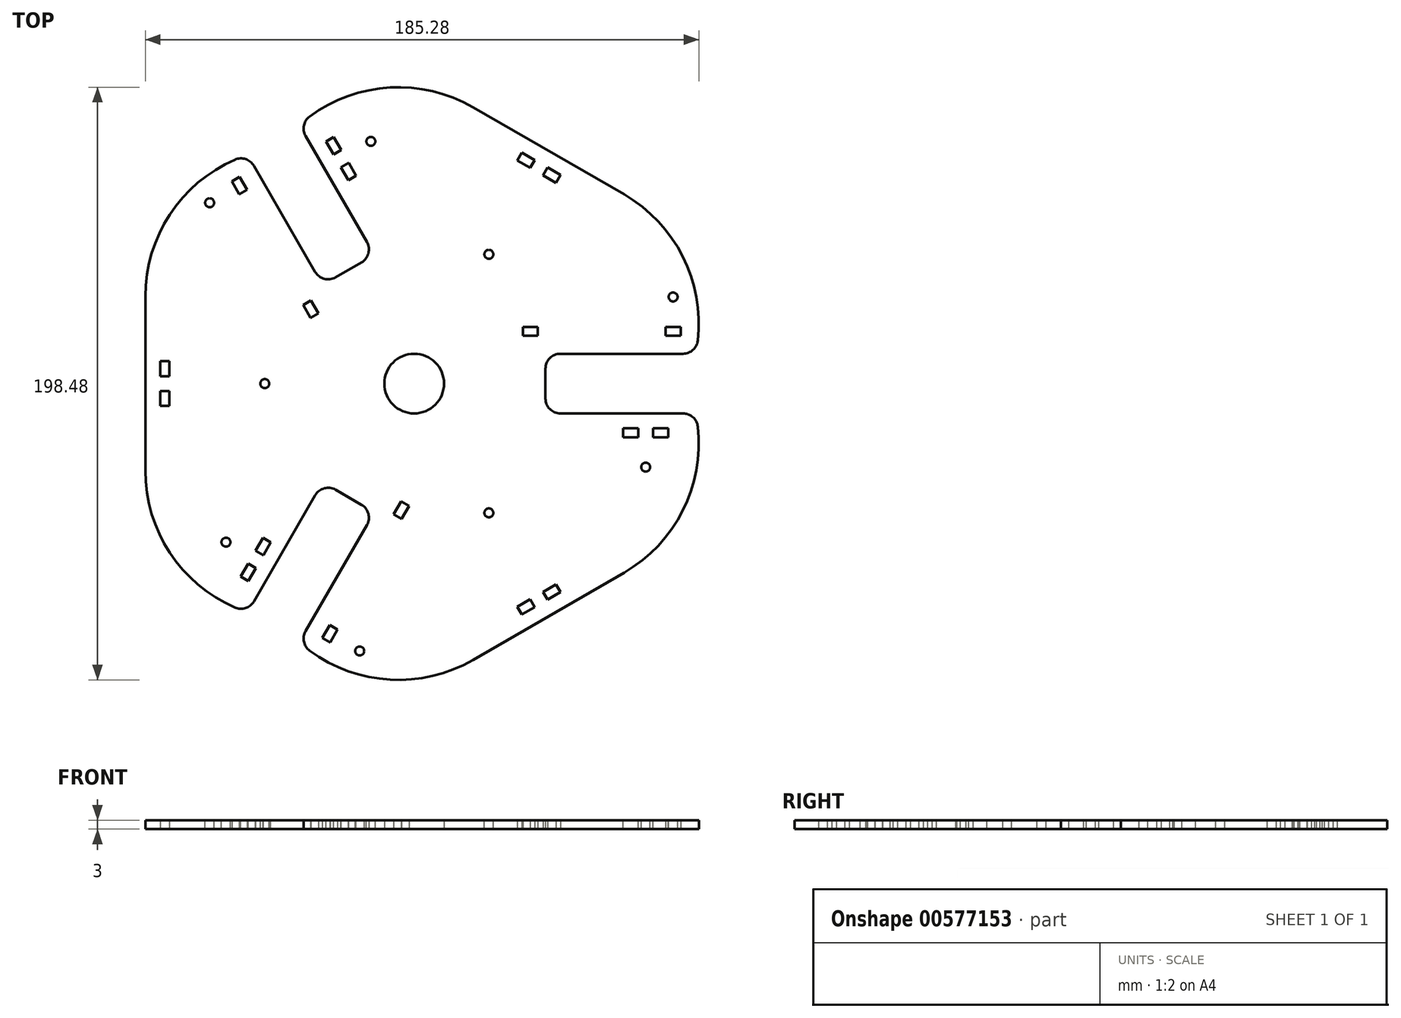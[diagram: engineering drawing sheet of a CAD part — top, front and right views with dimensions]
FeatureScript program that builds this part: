
annotation { "Feature Type Name" : "Feature", "Feature Type Description" : "" }
export const myFeature = defineFeature(function(context is Context, id is Id, definition is map)
    precondition{}
    {
        {
            var Q0;
            Q0=qCreatedBy(makeId("Top.planeOp"),FACE);
            var sketch = newSketch(context, id + "F0", { "sketchPlane" : qUnion([Q0])});
            skLineSegment(sketch, "E0", {"start": v(19.85, 17.5) * mm, "end": v(153.53, 17.5) * mm, "construction": true});
            skLineSegment(sketch, "E1.bottom", {"start": v(41.39, 16) * mm, "end": v(36.39, 16) * mm});
            skLineSegment(sketch, "E1.top", {"start": v(41.39, 19) * mm, "end": v(36.39, 19) * mm});
            skLineSegment(sketch, "E1.left", {"start": v(41.39, 16) * mm, "end": v(41.39, 19) * mm});
            skLineSegment(sketch, "E1.right", {"start": v(36.39, 16) * mm, "end": v(36.39, 19) * mm});
            skPoint(sketch, "E1.middle", {"position": v(38.89, 17.5) * mm});
            skLineSegment(sketch, "E2.bottom", {"start": v(89.19, 16) * mm, "end": v(84.19, 16) * mm});
            skLineSegment(sketch, "E2.top", {"start": v(89.19, 19) * mm, "end": v(84.19, 19) * mm});
            skLineSegment(sketch, "E2.left", {"start": v(89.19, 16) * mm, "end": v(89.19, 19) * mm});
            skLineSegment(sketch, "E2.right", {"start": v(84.19, 16) * mm, "end": v(84.19, 19) * mm});
            skPoint(sketch, "E2.middle", {"position": v(86.69, 17.5) * mm});
            skLineSegment(sketch, "E3", {"start": v(90, 10) * mm, "end": v(48.96, 10) * mm});
            skLineSegment(sketch, "E4", {"start": v(43.96, 5) * mm, "end": v(43.96, -5) * mm});
            skLineSegment(sketch, "E5", {"start": v(48.96, -10) * mm, "end": v(90, -10) * mm});
            skPoint(sketch, "E6.visualSharp", {"position": v(43.96, 10) * mm});
            skArc(sketch, "E6.filletArc", {"start": v(48.96, 10) * mm, "mid": v(45.42, 8.54) * mm, "end": v(43.96, 5) * mm});
            skPoint(sketch, "E7.visualSharp", {"position": v(43.96, -10) * mm});
            skArc(sketch, "E7.filletArc", {"start": v(43.96, -5) * mm, "mid": v(45.42, -8.54) * mm, "end": v(48.96, -10) * mm});
            skPoint(sketch, "E8.visualSharp", {"position": v(94.4, 59.99) * mm});
            skArc(sketch, "E8.filletArc", {"start": v(94.97, 14.44) * mm, "mid": v(89.92, 42.57) * mm, "end": v(70.28, 63.34) * mm});
            skPoint(sketch, "E9.visualSharp", {"position": v(94.34, 10) * mm});
            skArc(sketch, "E9.filletArc", {"start": v(90, 10) * mm, "mid": v(93.33, 11.27) * mm, "end": v(94.97, 14.44) * mm});
            skPoint(sketch, "E10.visualSharp", {"position": v(102.08, -10) * mm});
            skArc(sketch, "E10.filletArc", {"start": v(94.97, -14.44) * mm, "mid": v(93.33, -11.27) * mm, "end": v(90, -10) * mm});
            skLineSegment(sketch, "E11", {"start": v(0, 0) * mm, "end": v(57.44, 99.5) * mm, "construction": true});
            skLineSegment(sketch, "E12", {"start": v(0, 0) * mm, "end": v(55.62, -96.34) * mm, "construction": true});
            skLineSegment(sketch, "E13", {"start": v(70.28, -63.34) * mm, "end": v(45, -77.94) * mm});
            skLineSegment(sketch, "E14", {"start": v(70.28, 63.34) * mm, "end": v(45, 77.94) * mm});
            skPoint(sketch, "E15.visualSharp", {"position": v(93.21, -50.1) * mm});
            skArc(sketch, "E15.filletArc", {"start": v(70.28, -63.34) * mm, "mid": v(89.92, -42.57) * mm, "end": v(94.97, -14.44) * mm});
            skLineSegment(sketch, "E16.1.0", {"start": v(-90, 29.2) * mm, "end": v(-90, 0) * mm});
            skArc(sketch, "E16.1.1", {"start": v(-59.99, 75.03) * mm, "mid": v(-81.83, 56.59) * mm, "end": v(-90, 29.2) * mm});
            skArc(sketch, "E16.1.2", {"start": v(-53.66, 72.94) * mm, "mid": v(-56.43, 75.2) * mm, "end": v(-59.99, 75.03) * mm});
            skLineSegment(sketch, "E16.1.3", {"start": v(-53.66, 72.94) * mm, "end": v(-33.14, 37.4) * mm});
            skArc(sketch, "E16.1.4", {"start": v(-33.14, 37.4) * mm, "mid": v(-30.1, 35.07) * mm, "end": v(-26.3, 35.57) * mm});
            skLineSegment(sketch, "E16.1.5", {"start": v(-26.3, 35.57) * mm, "end": v(-17.65, 40.57) * mm});
            skArc(sketch, "E16.1.6", {"start": v(-17.65, 40.57) * mm, "mid": v(-15.32, 43.6) * mm, "end": v(-15.82, 47.4) * mm});
            skLineSegment(sketch, "E16.1.7", {"start": v(-15.82, 47.4) * mm, "end": v(-36.34, 82.94) * mm});
            skArc(sketch, "E16.1.8", {"start": v(19.72, 92.54) * mm, "mid": v(-8.09, 99.16) * mm, "end": v(-34.98, 89.46) * mm});
            skArc(sketch, "E16.1.9", {"start": v(-34.98, 89.46) * mm, "mid": v(-36.9, 86.46) * mm, "end": v(-36.34, 82.94) * mm});
            skLineSegment(sketch, "E16.1.10", {"start": v(-58.45, 69.24) * mm, "end": v(-55.95, 64.91) * mm});
            skLineSegment(sketch, "E16.1.11", {"start": v(-55.95, 64.91) * mm, "end": v(-58.55, 63.41) * mm});
            skLineSegment(sketch, "E16.1.12", {"start": v(-61.05, 67.74) * mm, "end": v(-58.55, 63.41) * mm});
            skLineSegment(sketch, "E16.1.13", {"start": v(-58.45, 69.24) * mm, "end": v(-61.05, 67.74) * mm});
            skLineSegment(sketch, "E16.1.14", {"start": v(-34.55, 27.84) * mm, "end": v(-37.15, 26.34) * mm});
            skLineSegment(sketch, "E16.1.15", {"start": v(-34.55, 27.84) * mm, "end": v(-32.05, 23.51) * mm});
            skLineSegment(sketch, "E16.1.16", {"start": v(-32.05, 23.51) * mm, "end": v(-34.65, 22.01) * mm});
            skLineSegment(sketch, "E16.1.17", {"start": v(-37.15, 26.34) * mm, "end": v(-34.65, 22.01) * mm});
            skLineSegment(sketch, "E16.1.18", {"start": v(19.72, 92.54) * mm, "end": v(45, 77.94) * mm});
            skLineSegment(sketch, "E16.2.0", {"start": v(19.72, -92.54) * mm, "end": v(45, -77.94) * mm});
            skArc(sketch, "E16.2.1", {"start": v(-34.98, -89.46) * mm, "mid": v(-8.09, -99.16) * mm, "end": v(19.72, -92.54) * mm});
            skArc(sketch, "E16.2.2", {"start": v(-36.34, -82.94) * mm, "mid": v(-36.9, -86.46) * mm, "end": v(-34.98, -89.46) * mm});
            skLineSegment(sketch, "E16.2.3", {"start": v(-36.34, -82.94) * mm, "end": v(-15.82, -47.4) * mm});
            skArc(sketch, "E16.2.4", {"start": v(-15.82, -47.4) * mm, "mid": v(-15.32, -43.6) * mm, "end": v(-17.65, -40.57) * mm});
            skLineSegment(sketch, "E16.2.5", {"start": v(-17.65, -40.57) * mm, "end": v(-26.3, -35.57) * mm});
            skArc(sketch, "E16.2.6", {"start": v(-26.3, -35.57) * mm, "mid": v(-30.1, -35.07) * mm, "end": v(-33.14, -37.4) * mm});
            skLineSegment(sketch, "E16.2.7", {"start": v(-33.14, -37.4) * mm, "end": v(-53.66, -72.94) * mm});
            skArc(sketch, "E16.2.8", {"start": v(-90, -29.2) * mm, "mid": v(-81.83, -56.59) * mm, "end": v(-59.99, -75.03) * mm});
            skArc(sketch, "E16.2.9", {"start": v(-59.99, -75.03) * mm, "mid": v(-56.43, -75.2) * mm, "end": v(-53.66, -72.94) * mm});
            skLineSegment(sketch, "E16.2.10", {"start": v(-30.74, -85.24) * mm, "end": v(-28.24, -80.91) * mm});
            skLineSegment(sketch, "E16.2.11", {"start": v(-28.24, -80.91) * mm, "end": v(-25.64, -82.41) * mm});
            skLineSegment(sketch, "E16.2.12", {"start": v(-28.14, -86.74) * mm, "end": v(-25.64, -82.41) * mm});
            skLineSegment(sketch, "E16.2.13", {"start": v(-30.74, -85.24) * mm, "end": v(-28.14, -86.74) * mm});
            skLineSegment(sketch, "E16.2.14", {"start": v(-6.84, -43.84) * mm, "end": v(-4.24, -45.34) * mm});
            skLineSegment(sketch, "E16.2.15", {"start": v(-6.84, -43.84) * mm, "end": v(-4.34, -39.51) * mm});
            skLineSegment(sketch, "E16.2.16", {"start": v(-4.34, -39.51) * mm, "end": v(-1.74, -41.01) * mm});
            skLineSegment(sketch, "E16.2.17", {"start": v(-4.24, -45.34) * mm, "end": v(-1.74, -41.01) * mm});
            skLineSegment(sketch, "E16.2.18", {"start": v(-90, -29.2) * mm, "end": v(-90, 0) * mm});
            skPoint(sketch, "E16.center", {"position": v(0, 0) * mm});
            skCircle(sketch, "E17", {"center": v(0, 0) * mm, "radius": 10 * mm});
            skLineSegment(sketch, "E18.bottom", {"start": v(-85, 7.5) * mm, "end": v(-82, 7.5) * mm});
            skLineSegment(sketch, "E18.top", {"start": v(-85, 2.5) * mm, "end": v(-82, 2.5) * mm});
            skLineSegment(sketch, "E18.left", {"start": v(-85, 7.5) * mm, "end": v(-85, 2.5) * mm});
            skLineSegment(sketch, "E18.right", {"start": v(-82, 7.5) * mm, "end": v(-82, 2.5) * mm});
            skLineSegment(sketch, "E19.bottom", {"start": v(-85, -2.5) * mm, "end": v(-82, -2.5) * mm});
            skLineSegment(sketch, "E19.top", {"start": v(-85, -7.5) * mm, "end": v(-82, -7.5) * mm});
            skLineSegment(sketch, "E19.left", {"start": v(-85, -2.5) * mm, "end": v(-85, -7.5) * mm});
            skLineSegment(sketch, "E19.right", {"start": v(-82, -2.5) * mm, "end": v(-82, -7.5) * mm});
            skLineSegment(sketch, "E20.1.0", {"start": v(36, -77.36) * mm, "end": v(34.5, -74.76) * mm});
            skLineSegment(sketch, "E20.1.1", {"start": v(36, -77.36) * mm, "end": v(40.33, -74.86) * mm});
            skLineSegment(sketch, "E20.1.2", {"start": v(34.5, -74.76) * mm, "end": v(38.83, -72.26) * mm});
            skLineSegment(sketch, "E20.1.3", {"start": v(40.33, -74.86) * mm, "end": v(38.83, -72.26) * mm});
            skLineSegment(sketch, "E20.1.4", {"start": v(44.67, -72.36) * mm, "end": v(43.17, -69.76) * mm});
            skLineSegment(sketch, "E20.1.5", {"start": v(44.67, -72.36) * mm, "end": v(49, -69.86) * mm});
            skLineSegment(sketch, "E20.1.6", {"start": v(49, -69.86) * mm, "end": v(47.5, -67.26) * mm});
            skLineSegment(sketch, "E20.1.7", {"start": v(43.17, -69.76) * mm, "end": v(47.5, -67.26) * mm});
            skLineSegment(sketch, "E20.2.0", {"start": v(49, 69.86) * mm, "end": v(47.5, 67.26) * mm});
            skLineSegment(sketch, "E20.2.1", {"start": v(49, 69.86) * mm, "end": v(44.67, 72.36) * mm});
            skLineSegment(sketch, "E20.2.2", {"start": v(47.5, 67.26) * mm, "end": v(43.17, 69.76) * mm});
            skLineSegment(sketch, "E20.2.3", {"start": v(44.67, 72.36) * mm, "end": v(43.17, 69.76) * mm});
            skLineSegment(sketch, "E20.2.4", {"start": v(40.33, 74.86) * mm, "end": v(38.83, 72.26) * mm});
            skLineSegment(sketch, "E20.2.5", {"start": v(40.33, 74.86) * mm, "end": v(36, 77.36) * mm});
            skLineSegment(sketch, "E20.2.6", {"start": v(36, 77.36) * mm, "end": v(34.5, 74.76) * mm});
            skLineSegment(sketch, "E20.2.7", {"start": v(38.83, 72.26) * mm, "end": v(34.5, 74.76) * mm});
            skSolve(sketch);
        }
        {
            var Q0;
            Q0=qSketchRegion(id+"F0",true);
            extrude(context, id + "F1", {"entities" : qUnion([Q0]), "depth" : 3 * mm});
        }
        {
            var Q0;
            Q0=makeQuery(id+"F1.opExtrude","CAP_FACE",FACE,{"disambiguationData":[OSD([sQuery(id+"F0.wireOp",EDGE,"E1.bottom"),sQuery(id+"F0.wireOp",EDGE,"E1.top"),sQuery(id+"F0.wireOp",EDGE,"E1.left"),sQuery(id+"F0.wireOp",EDGE,"E1.right"),sQuery(id+"F0.wireOp",EDGE,"E2.bottom"),sQuery(id+"F0.wireOp",EDGE,"E2.top"),sQuery(id+"F0.wireOp",EDGE,"E2.left"),sQuery(id+"F0.wireOp",EDGE,"E2.right"),sQuery(id+"F0.wireOp",EDGE,"E3"),sQuery(id+"F0.wireOp",EDGE,"E4"),sQuery(id+"F0.wireOp",EDGE,"E5"),sQuery(id+"F0.wireOp",EDGE,"E6.filletArc"),sQuery(id+"F0.wireOp",EDGE,"E7.filletArc"),sQuery(id+"F0.wireOp",EDGE,"E8.filletArc"),sQuery(id+"F0.wireOp",EDGE,"E9.filletArc"),sQuery(id+"F0.wireOp",EDGE,"E10.filletArc"),sQuery(id+"F0.wireOp",EDGE,"E13"),sQuery(id+"F0.wireOp",EDGE,"E14"),sQuery(id+"F0.wireOp",EDGE,"E15.filletArc"),sQuery(id+"F0.wireOp",EDGE,"E16.1.0"),sQuery(id+"F0.wireOp",EDGE,"E16.1.1"),sQuery(id+"F0.wireOp",EDGE,"E16.1.2"),sQuery(id+"F0.wireOp",EDGE,"E16.1.3"),sQuery(id+"F0.wireOp",EDGE,"E16.1.4"),sQuery(id+"F0.wireOp",EDGE,"E16.1.5"),sQuery(id+"F0.wireOp",EDGE,"E16.1.6"),sQuery(id+"F0.wireOp",EDGE,"E16.1.7"),sQuery(id+"F0.wireOp",EDGE,"E16.1.8"),sQuery(id+"F0.wireOp",EDGE,"E16.1.9"),sQuery(id+"F0.wireOp",EDGE,"E16.1.10"),sQuery(id+"F0.wireOp",EDGE,"E16.1.11"),sQuery(id+"F0.wireOp",EDGE,"E16.1.12"),sQuery(id+"F0.wireOp",EDGE,"E16.1.13"),sQuery(id+"F0.wireOp",EDGE,"E16.1.14"),sQuery(id+"F0.wireOp",EDGE,"E16.1.15"),sQuery(id+"F0.wireOp",EDGE,"E16.1.16"),sQuery(id+"F0.wireOp",EDGE,"E16.1.17"),sQuery(id+"F0.wireOp",EDGE,"E16.1.18"),sQuery(id+"F0.wireOp",EDGE,"E16.2.0"),sQuery(id+"F0.wireOp",EDGE,"E16.2.1"),sQuery(id+"F0.wireOp",EDGE,"E16.2.2"),sQuery(id+"F0.wireOp",EDGE,"E16.2.3"),sQuery(id+"F0.wireOp",EDGE,"E16.2.4"),sQuery(id+"F0.wireOp",EDGE,"E16.2.5"),sQuery(id+"F0.wireOp",EDGE,"E16.2.6"),sQuery(id+"F0.wireOp",EDGE,"E16.2.7"),sQuery(id+"F0.wireOp",EDGE,"E16.2.8"),sQuery(id+"F0.wireOp",EDGE,"E16.2.9"),sQuery(id+"F0.wireOp",EDGE,"E16.2.10"),sQuery(id+"F0.wireOp",EDGE,"E16.2.11"),sQuery(id+"F0.wireOp",EDGE,"E16.2.12"),sQuery(id+"F0.wireOp",EDGE,"E16.2.13"),sQuery(id+"F0.wireOp",EDGE,"E16.2.14"),sQuery(id+"F0.wireOp",EDGE,"E16.2.15"),sQuery(id+"F0.wireOp",EDGE,"E16.2.16"),sQuery(id+"F0.wireOp",EDGE,"E16.2.17"),sQuery(id+"F0.wireOp",EDGE,"E16.2.18"),sQuery(id+"F0.wireOp",EDGE,"E17"),sQuery(id+"F0.wireOp",EDGE,"E18.bottom"),sQuery(id+"F0.wireOp",EDGE,"E18.top"),sQuery(id+"F0.wireOp",EDGE,"E18.left"),sQuery(id+"F0.wireOp",EDGE,"E18.right"),sQuery(id+"F0.wireOp",EDGE,"E19.bottom"),sQuery(id+"F0.wireOp",EDGE,"E19.top"),sQuery(id+"F0.wireOp",EDGE,"E19.left"),sQuery(id+"F0.wireOp",EDGE,"E19.right"),sQuery(id+"F0.wireOp",EDGE,"E20.1.0"),sQuery(id+"F0.wireOp",EDGE,"E20.1.1"),sQuery(id+"F0.wireOp",EDGE,"E20.1.2"),sQuery(id+"F0.wireOp",EDGE,"E20.1.3"),sQuery(id+"F0.wireOp",EDGE,"E20.1.4"),sQuery(id+"F0.wireOp",EDGE,"E20.1.5"),sQuery(id+"F0.wireOp",EDGE,"E20.1.6"),sQuery(id+"F0.wireOp",EDGE,"E20.1.7"),sQuery(id+"F0.wireOp",EDGE,"E20.2.0"),sQuery(id+"F0.wireOp",EDGE,"E20.2.1"),sQuery(id+"F0.wireOp",EDGE,"E20.2.2"),sQuery(id+"F0.wireOp",EDGE,"E20.2.3"),sQuery(id+"F0.wireOp",EDGE,"E20.2.4"),sQuery(id+"F0.wireOp",EDGE,"E20.2.5"),sQuery(id+"F0.wireOp",EDGE,"E20.2.6"),sQuery(id+"F0.wireOp",EDGE,"E20.2.7")])],"isStart":false});
            var sketch = newSketch(context, id + "F2", { "sketchPlane" : qUnion([Q0])});
            skCircle(sketch, "E21", {"center": v(-50, 0) * mm, "radius": 1.5 * mm});
            skCircle(sketch, "E22.1.0", {"center": v(25, -43.3) * mm, "radius": 1.5 * mm});
            skCircle(sketch, "E22.2.0", {"center": v(25, 43.3) * mm, "radius": 1.5 * mm});
            skPoint(sketch, "E22.center", {"position": v(0, 0) * mm});
            skCircle(sketch, "E23", {"center": v(86.69, 29) * mm, "radius": 1.5 * mm});
            skPoint(sketch, "E23.centerSnap0", {"position": v(86.69, 19) * mm});
            skCircle(sketch, "E24.1.0", {"center": v(-68.46, 60.58) * mm, "radius": 1.5 * mm});
            skCircle(sketch, "E24.2.0", {"center": v(-18.23, -89.58) * mm, "radius": 1.5 * mm});
            skLineSegment(sketch, "E25.bottom", {"start": v(70, -15) * mm, "end": v(75, -15) * mm});
            skLineSegment(sketch, "E25.top", {"start": v(70, -18) * mm, "end": v(75, -18) * mm});
            skLineSegment(sketch, "E25.left", {"start": v(70, -15) * mm, "end": v(70, -18) * mm});
            skLineSegment(sketch, "E25.right", {"start": v(75, -15) * mm, "end": v(75, -18) * mm});
            skLineSegment(sketch, "E26.bottom", {"start": v(80, -15) * mm, "end": v(85, -15) * mm});
            skLineSegment(sketch, "E26.top", {"start": v(80, -18) * mm, "end": v(85, -18) * mm});
            skLineSegment(sketch, "E26.left", {"start": v(80, -15) * mm, "end": v(80, -18) * mm});
            skLineSegment(sketch, "E26.right", {"start": v(85, -15) * mm, "end": v(85, -18) * mm});
            skLineSegment(sketch, "E27.1.0", {"start": v(-22, 68.12) * mm, "end": v(-24.5, 72.45) * mm});
            skLineSegment(sketch, "E27.1.1", {"start": v(-22, 68.12) * mm, "end": v(-19.41, 69.62) * mm});
            skLineSegment(sketch, "E27.1.2", {"start": v(-19.41, 69.62) * mm, "end": v(-21.91, 73.95) * mm});
            skLineSegment(sketch, "E27.1.3", {"start": v(-24.5, 72.45) * mm, "end": v(-21.91, 73.95) * mm});
            skLineSegment(sketch, "E27.1.4", {"start": v(-27, 76.78) * mm, "end": v(-24.41, 78.28) * mm});
            skLineSegment(sketch, "E27.1.5", {"start": v(-27, 76.78) * mm, "end": v(-29.5, 81.11) * mm});
            skLineSegment(sketch, "E27.1.6", {"start": v(-29.5, 81.11) * mm, "end": v(-26.91, 82.61) * mm});
            skLineSegment(sketch, "E27.1.7", {"start": v(-24.41, 78.28) * mm, "end": v(-26.91, 82.61) * mm});
            skLineSegment(sketch, "E27.2.0", {"start": v(-48, -53.12) * mm, "end": v(-50.5, -57.45) * mm});
            skLineSegment(sketch, "E27.2.1", {"start": v(-48, -53.12) * mm, "end": v(-50.59, -51.62) * mm});
            skLineSegment(sketch, "E27.2.2", {"start": v(-50.59, -51.62) * mm, "end": v(-53.09, -55.95) * mm});
            skLineSegment(sketch, "E27.2.3", {"start": v(-50.5, -57.45) * mm, "end": v(-53.09, -55.95) * mm});
            skLineSegment(sketch, "E27.2.4", {"start": v(-53, -61.78) * mm, "end": v(-55.59, -60.28) * mm});
            skLineSegment(sketch, "E27.2.5", {"start": v(-53, -61.78) * mm, "end": v(-55.5, -66.11) * mm});
            skLineSegment(sketch, "E27.2.6", {"start": v(-55.5, -66.11) * mm, "end": v(-58.09, -64.61) * mm});
            skLineSegment(sketch, "E27.2.7", {"start": v(-55.59, -60.28) * mm, "end": v(-58.09, -64.61) * mm});
            skCircle(sketch, "E28", {"center": v(77.5, -28) * mm, "radius": 1.5 * mm});
            skCircle(sketch, "E29.1.0", {"center": v(-14.5, 81.12) * mm, "radius": 1.5 * mm});
            skCircle(sketch, "E29.2.0", {"center": v(-63, -53.12) * mm, "radius": 1.5 * mm});
            skSolve(sketch);
        }
        {
            var Q0;
            Q0=qSketchRegion(id+"F2",true);
            extrude(context, id + "F3", {"entities" : qUnion([Q0]), "operationType" : NewBodyOperationType.REMOVE, "endBound" : BoundingType.UP_TO_NEXT, "oppositeDirection" : true, "depth" : 25 * mm});
        }
    });
